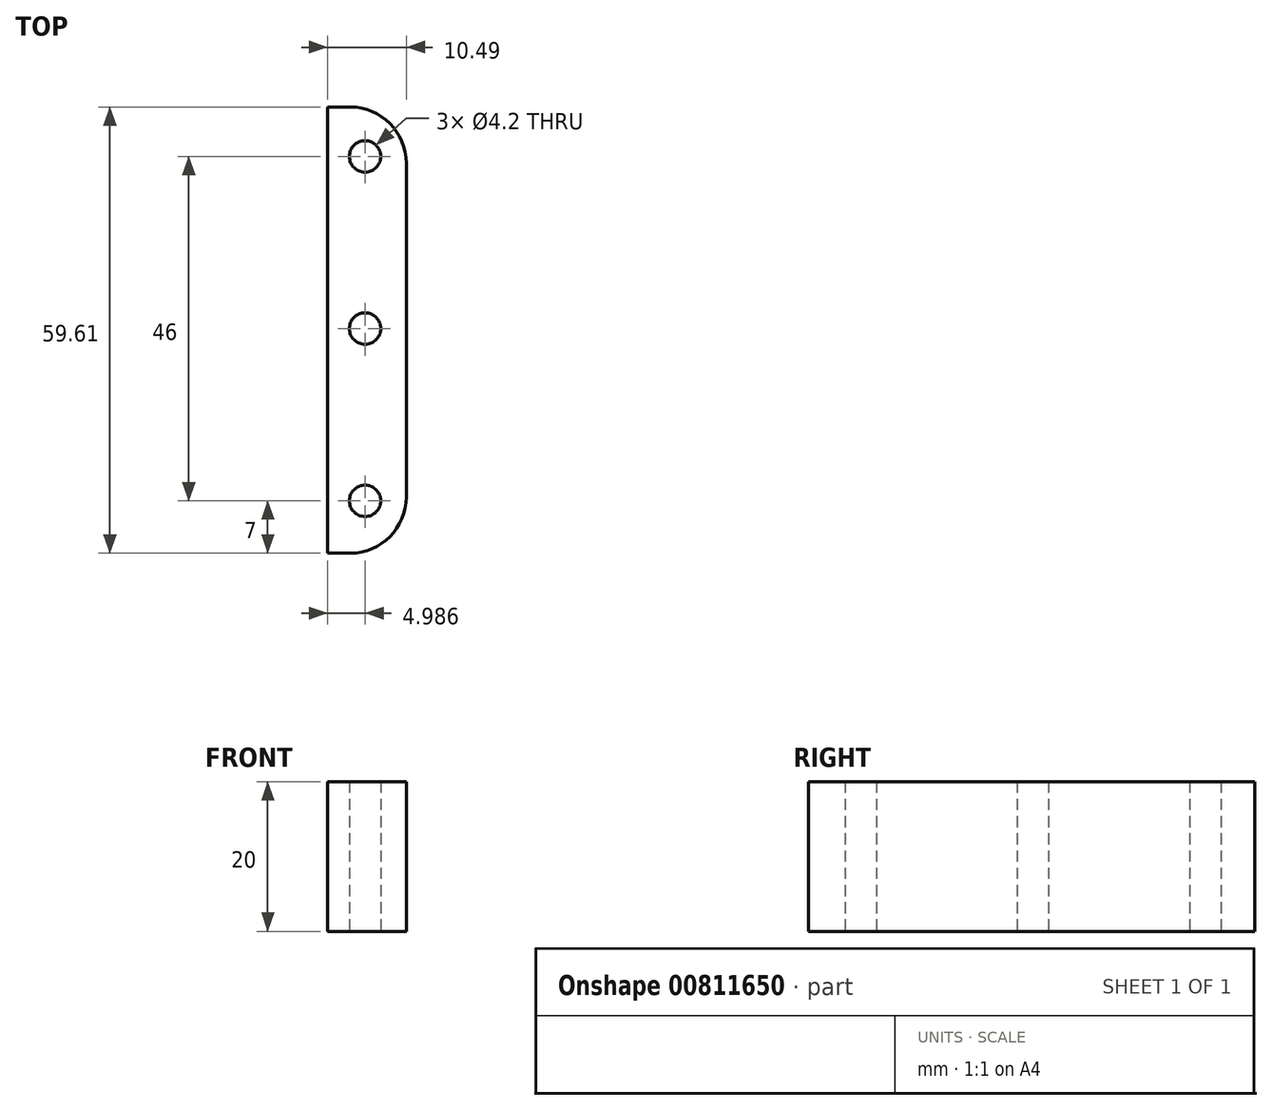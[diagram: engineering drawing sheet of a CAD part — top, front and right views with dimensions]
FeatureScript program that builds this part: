
annotation { "Feature Type Name" : "Feature", "Feature Type Description" : "" }
export const myFeature = defineFeature(function(context is Context, id is Id, definition is map)
    precondition{}
    {
        {
            var Q0;
            Q0=qCreatedBy(makeId("Top.planeOp"),FACE);
            var sketch = newSketch(context, id + "F0", { "sketchPlane" : qUnion([Q0])});
            skFitSpline(sketch, "E0.1", {"points": [v(112.45, 0) * mm, v(76.63, 0) * mm, v(40.82, 0) * mm, v(5, 0) * mm]});
            skFitSpline(sketch, "E0.2", {"points": [v(10, 5) * mm, v(10, 8.25) * mm, v(10, 11.5) * mm, v(10, 14.75) * mm]});
            skFitSpline(sketch, "E0.3", {"points": [v(15, 19.75) * mm, v(17.53, 19.75) * mm, v(20.06, 19.75) * mm, v(22.6, 19.75) * mm]});
            skFitSpline(sketch, "E0.4", {"points": [v(29.93, 24.75) * mm, v(29.93, 28.02) * mm, v(29.93, 31.3) * mm, v(29.93, 34.57) * mm]});
            skFitSpline(sketch, "E0.5", {"points": [v(34.93, 39.57) * mm, v(37.47, 39.57) * mm, v(40, 39.57) * mm, v(42.54, 39.57) * mm]});
            skLineSegment(sketch, "E1", {"start": v(38.2, 31.92) * mm, "end": v(38.2, 27.67) * mm, "construction": true});
            skCircle(sketch, "E2", {"center": v(38.2, 29.8) * mm, "radius": 2 * mm});
            skLineSegment(sketch, "E3", {"start": v(38.2, 11.92) * mm, "end": v(38.2, 7.67) * mm, "construction": true});
            skCircle(sketch, "E4", {"center": v(38.2, 9.8) * mm, "radius": 2 * mm});
            skLineSegment(sketch, "E5", {"start": v(18.23, 11.92) * mm, "end": v(18.23, 7.67) * mm, "construction": true});
            skCircle(sketch, "E6", {"center": v(18.23, 9.8) * mm, "radius": 2 * mm});
            skLineSegment(sketch, "E7", {"start": v(29.93, 24.75) * mm, "end": v(29.93, 24.75) * mm});
            skLineSegment(sketch, "E8", {"start": v(24.93, 19.75) * mm, "end": v(22.6, 19.75) * mm});
            skPoint(sketch, "E9.visualSharp", {"position": v(29.93, 39.57) * mm});
            skArc(sketch, "E9.filletArc", {"start": v(34.93, 39.57) * mm, "mid": v(31.4, 38.1) * mm, "end": v(29.93, 34.57) * mm});
            skPoint(sketch, "E10.visualSharp", {"position": v(29.93, 19.75) * mm});
            skArc(sketch, "E10.filletArc", {"start": v(24.93, 19.75) * mm, "mid": v(28.46, 21.21) * mm, "end": v(29.93, 24.75) * mm});
            skPoint(sketch, "E11.visualSharp", {"position": v(10, 19.75) * mm});
            skArc(sketch, "E11.filletArc", {"start": v(15, 19.75) * mm, "mid": v(11.46, 18.28) * mm, "end": v(10, 14.75) * mm});
            skArc(sketch, "E12.filletArc", {"start": v(10, 5) * mm, "mid": v(11.46, 1.46) * mm, "end": v(15, 0) * mm});
            skLineSegment(sketch, "E13", {"start": v(105.96, 42.26) * mm, "end": v(102.92, 42.26) * mm, "construction": true});
            skLineSegment(sketch, "E14", {"start": v(105.95, 11.35) * mm, "end": v(102.92, 11.35) * mm, "construction": true});
            skLineSegment(sketch, "E15", {"start": v(76.77, 26.74) * mm, "end": v(101.1, 26.74) * mm, "construction": true});
            skLineSegment(sketch, "E16", {"start": v(88.93, 26.74) * mm, "end": v(88.93, 14.58) * mm, "construction": true});
            skLineSegment(sketch, "E17", {"start": v(88.93, 26.74) * mm, "end": v(88.93, 38.9) * mm, "construction": true});
            skCircle(sketch, "E18", {"center": v(88.93, 26.74) * mm, "radius": 12.12 * mm});
            skCircle(sketch, "E19", {"center": v(104.44, 42.26) * mm, "radius": 1.5 * mm});
            skCircle(sketch, "E20", {"center": v(73.33, 42.26) * mm, "radius": 1.5 * mm});
            skCircle(sketch, "E21", {"center": v(73.33, 11.27) * mm, "radius": 1.5 * mm});
            skCircle(sketch, "E22", {"center": v(104.44, 11.35) * mm, "radius": 1.5 * mm});
            skPoint(sketch, "E23.startSnap0", {"position": v(71.76, 26.8) * mm});
            skPoint(sketch, "E24.visualSharp", {"position": v(120.45, 48.62) * mm});
            skArc(sketch, "E24.filletArc", {"start": v(120.45, 40.62) * mm, "mid": v(118.1, 46.28) * mm, "end": v(112.45, 48.62) * mm});
            skLineSegment(sketch, "E25", {"start": v(120.45, 41.12) * mm, "end": v(120.45, 8) * mm});
            skPoint(sketch, "E26.visualSharp", {"position": v(120.45, 0) * mm});
            skArc(sketch, "E26.filletArc", {"start": v(112.45, 0) * mm, "mid": v(118.1, 2.34) * mm, "end": v(120.45, 8) * mm});
            skCircle(sketch, "E27.0", {"center": v(114.95, 8.3) * mm, "radius": 2 * mm});
            skCircle(sketch, "E27.1", {"center": v(114.95, 24.3) * mm, "radius": 2 * mm});
            skCircle(sketch, "E27.2", {"center": v(114.95, 40.3) * mm, "radius": 2 * mm});
            skLineSegment(sketch, "E28", {"start": v(112.45, 48.62) * mm, "end": v(64.3, 48.62) * mm});
            skFitSpline(sketch, "E29", {"points": [v(42.54, 39.57) * mm, v(52.68, 43.84) * mm, v(64.3, 48.62) * mm], "startDerivative": vector(30.66, -0.07) * mm, "endDerivative": vector(25.74, 1.13) * mm});
            skSolve(sketch);
        }
        {
            var Q0;
            Q0=qCreatedBy(makeId("Top.planeOp"),FACE);
            var sketch = newSketch(context, id + "F1", { "sketchPlane" : qUnion([Q0])});
            skLineSegment(sketch, "E30.0", {"start": v(109.46, 59.6) * mm, "end": v(109.46, 0) * mm});
            skArc(sketch, "E30.1", {"start": v(119.95, 52.1) * mm, "mid": v(117.75, 57.41) * mm, "end": v(112.45, 59.6) * mm});
            skFitSpline(sketch, "E30.2", {"points": [v(119.95, 52.1) * mm, v(119.95, 37.24) * mm, v(119.95, 22.37) * mm, v(119.95, 7.5) * mm]});
            skArc(sketch, "E30.3", {"start": v(112.45, 0) * mm, "mid": v(117.75, 2.2) * mm, "end": v(119.95, 7.5) * mm});
            skCircle(sketch, "E30.4", {"center": v(114.45, 7) * mm, "radius": 2 * mm, "construction": true});
            skCircle(sketch, "E30.5", {"center": v(114.45, 30) * mm, "radius": 2.1 * mm});
            skCircle(sketch, "E30.6", {"center": v(114.45, 53) * mm, "radius": 2 * mm, "construction": true});
            skLineSegment(sketch, "E31", {"start": v(109.46, 59.6) * mm, "end": v(112.45, 59.6) * mm});
            skLineSegment(sketch, "E32", {"start": v(109.46, 0) * mm, "end": v(112.45, 0) * mm});
            skCircle(sketch, "E33", {"center": v(114.45, 53) * mm, "radius": 2.1 * mm});
            skCircle(sketch, "E34", {"center": v(114.45, 7) * mm, "radius": 2.1 * mm});
            skSolve(sketch);
        }
        {
            var Q0;
            Q0=makeQuery(id+"F1.imprint","IMPRINT",FACE,{"disambiguationData":[TD([[makeQuery(id+"F1.imprint","IMPRINT",EDGE,{"derivedFrom":sQuery(id+"F1.wireOp",EDGE,"E30.0")}),1.0]])]});
            extrude(context, id + "F2", {"entities" : qUnion([Q0]), "depth" : 20 * mm, "offsetDistance" : 25 * mm});
        }
    });
